# Revit family: Spout-American_Standard-Tub Spout-888811X
name_source: partatom
category: Plumbing Fixtures
revit_build: Autodesk Revit 2014 (Build: 20130308_1515(x64)
units: mm (PartAtom-declared; Revit-internal decimal feet)

## types (2) — shared parameters
Assembly Code = D2020300
CW Connection = Yes
CWFU = 3
Default Elevation = 21"
Finish = Metal-American Standard-002-Polished Chrome
HW Connection = Yes
HWFU = 3
Height = 2 5/8"
Installation Type = Wall Mounted
Length = 7 5/16"
Manufacturer = American Standard
Material = Metal-American Standard-002-Polished Chrome
Price = Prices may vary. Please consult Manufacturer Representative for most up-to-date price list.
Product Documentation Link = https://www.americanstandard-us.com
Product Page URL = https://www.americanstandard-us.com
URL = https://www.americanstandard-us.com
Vent Connection = No
WFU = 4
Warranty Information = Limited Lifetime Function and Finish Warranty
Waste Connection = No
Water Connection Diameter = 1/2"
Water Connection Radius = 1/4"
Width = 2 5/8"

## per-type parameters (varying)
| type | Connection Description | Description |
| 8888110 | 1/2" Slip-On Supply Inlet | Slip-On Non-Diverter Tub Spout |
| 8888111 | 1/2" IPS Supply Inlet | Non-Diverter 1/2" IPS Tub Spout |

note: column(s) folded — value = type name in every type: Model

## geometry (parser evidence)
native form markers: Sweep x3
no freeform markers — native parametric forms only
